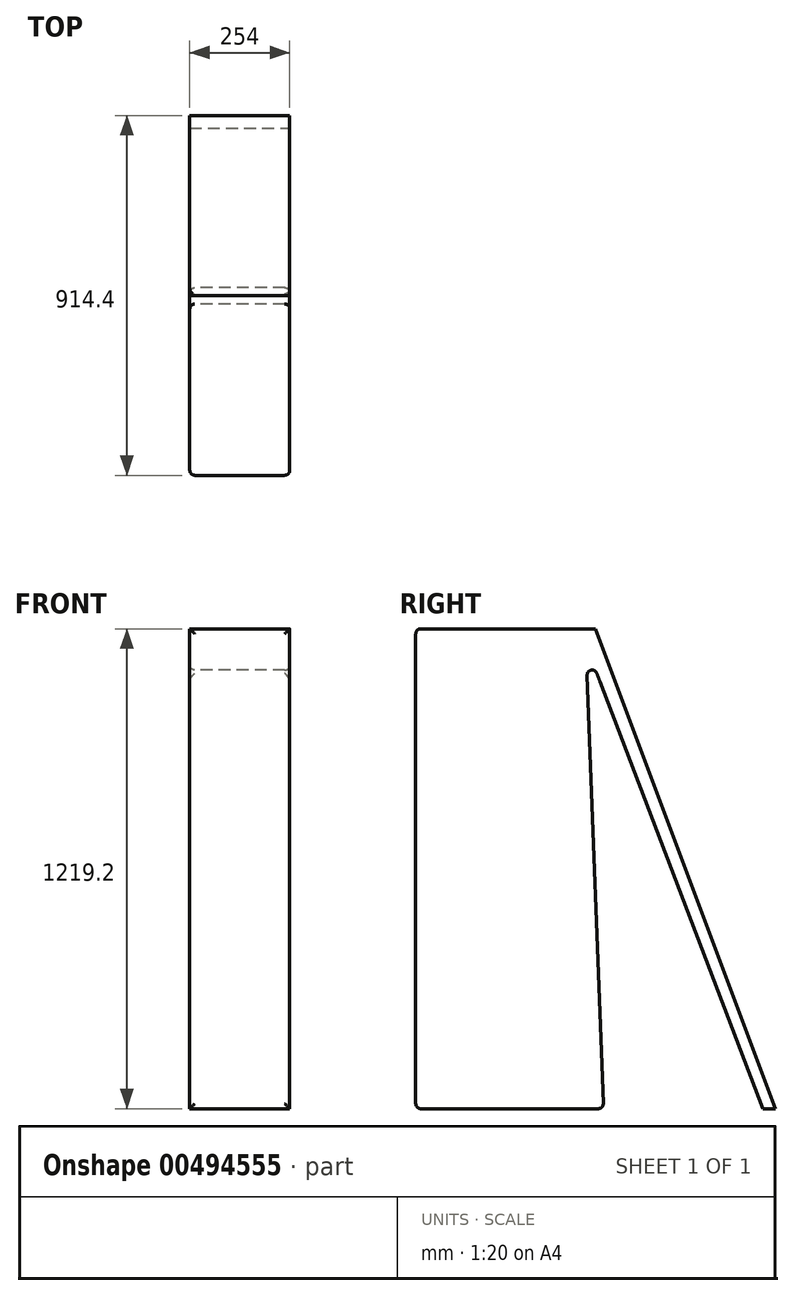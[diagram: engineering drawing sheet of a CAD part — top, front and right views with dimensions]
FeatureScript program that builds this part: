
annotation { "Feature Type Name" : "Feature", "Feature Type Description" : "" }
export const myFeature = defineFeature(function(context is Context, id is Id, definition is map)
    precondition{}
    {
        {
            var Q0;
            Q0=qCreatedBy(makeId("Front.planeOp"),FACE);
            var sketch = newSketch(context, id + "F0", { "sketchPlane" : qUnion([Q0])});
            skLineSegment(sketch, "E0.bottom", {"start": v(0, 0) * mm, "end": v(-254, 0) * mm});
            skLineSegment(sketch, "E0.top", {"start": v(0, 1219.2) * mm, "end": v(-254, 1219.2) * mm});
            skLineSegment(sketch, "E0.left", {"start": v(0, 0) * mm, "end": v(0, 1219.2) * mm});
            skLineSegment(sketch, "E0.right", {"start": v(-254, 0) * mm, "end": v(-254, 1219.2) * mm});
            skSolve(sketch);
        }
        {
            var Q0;
            Q0 = qSketchRegion(id + "F0", true);
            extrude(context, id + "F1", {"entities" : qUnion([Q0]), "depth" : 914.4 * mm});
        }
        {
            var Q0;
            Q0=qCreatedBy(makeId("Right.planeOp"),FACE);
            var sketch = newSketch(context, id + "F2", { "sketchPlane" : qUnion([Q0])});
            skLineSegment(sketch, "E1", {"start": v(0, 0) * mm, "end": v(-462.4, 1231.04) * mm});
            skLineSegment(sketch, "E2", {"start": v(-462.4, 1231.04) * mm, "end": v(0, 1231.04) * mm});
            skLineSegment(sketch, "E3", {"start": v(0, 1231.04) * mm, "end": v(0, 0) * mm});
            skSolve(sketch);
        }
        {
            var Q0;
            Q0 = qSketchRegion(id + "F2", true);
            extrude(context, id + "F3", {"entities" : qUnion([Q0]), "operationType" : NewBodyOperationType.REMOVE, "endBound" : BoundingType.THROUGH_ALL, "oppositeDirection" : true, "depth" : -304.8 * mm});
        }
        {
            var Q0;
            Q0=qCreatedBy(makeId("Right.planeOp"),FACE);
            var sketch = newSketch(context, id + "F4", { "sketchPlane" : qUnion([Q0])});
            skLineSegment(sketch, "E4", {"start": v(-32.03, 0) * mm, "end": v(-481.87, 1178) * mm});
            skLineSegment(sketch, "E5", {"start": v(-481.87, 1178) * mm, "end": v(-437.48, 0) * mm});
            skLineSegment(sketch, "E6", {"start": v(-437.48, 0) * mm, "end": v(-32.03, 0) * mm});
            skSolve(sketch);
        }
        {
            var Q0;
            Q0 = qSketchRegion(id + "F4", true);
            extrude(context, id + "F5", {"entities" : qUnion([Q0]), "operationType" : NewBodyOperationType.REMOVE, "endBound" : BoundingType.THROUGH_ALL, "oppositeDirection" : true, "depth" : -304.8 * mm});
        }
        {
            var Q0;
            Q0=makeQuery(id+"F1.opExtrude","CAP_FACE",FACE,{"disambiguationData":[OSD([sQuery(id+"F0.wireOp",EDGE,"E0.bottom"),sQuery(id+"F0.wireOp",EDGE,"E0.top"),sQuery(id+"F0.wireOp",EDGE,"E0.left"),sQuery(id+"F0.wireOp",EDGE,"E0.right")])],"isStart":false});
            var Q1;
            Q1=makeQuery(id+"F5.boolean.opBoolean","COPY",FACE,{"derivedFrom":makeQuery(id+"F5.opExtrude","SWEPT_FACE",FACE,{"disambiguationData":[OSD([sQuery(id+"F4.wireOp",EDGE,"E5")])]})});
            fillet(context, id + "F6", {"entities" : qUnion([Q0, Q1]), "radius" : 12.7 * mm, "tangentPropagation" : true, "allowEdgeOverflow" : false});
        }
    });
